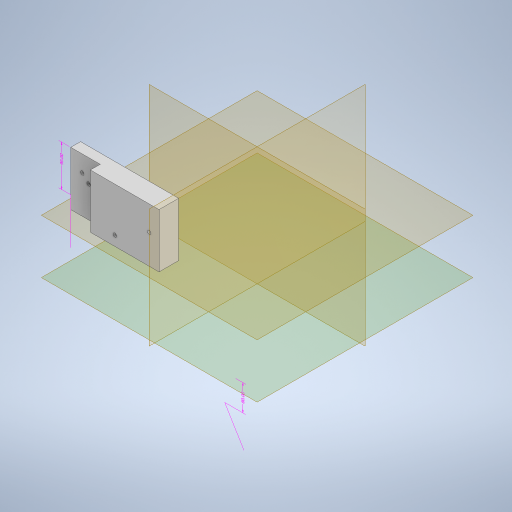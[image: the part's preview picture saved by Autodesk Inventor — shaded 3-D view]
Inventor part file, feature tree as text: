
AUTODESK INVENTOR PART (.ipt)
format: ipt  version: 2023 (Build 270158000, 158)  size: 438,272 bytes
history: native  units: mm
features: sketch x9, other x5, extrude x5, split x5, hole x4, plane x4
ambient origin geometry x8: Origin, YZ Plane, XZ Plane, XY Plane, X Axis, Y Axis, Z Axis, Center Point
bodies: Body1 (feature_tree)
feature tree (32):
  other  "Sólido1"
  other  "Anotaciones"
  extrude  "Extrusión1"  Depth=200.0mm
  hole  "Agujero1"  [1 undecoded]
  extrude  "Extrusión2"  Depth=15.0mm
  extrude  "Extrusión3"  Depth=20.0mm TaperAngle=0.0deg
  extrude  "Extrusión4"  Depth=200.0mm
  extrude  "Extrusión5"  Depth=20.0mm
  hole  "Agujero2"  [1 undecoded]
  plane  "Plano de trabajo1"
  split  "Dividir1"
  plane  "Plano de trabajo2"
  plane  "Plano de trabajo3"
  sketch  "Boceto9"  dims[d37=20.0mm d38=20.0mm]
  plane  "Plano de trabajo4"
  hole  "Agujero3"  [1 undecoded]
  hole  "Agujero4"  [1 undecoded]
  split  "Dividir2"
  split  "Dividir3"
  split  "Dividir4"
  split  "Dividir5"
  other  "Suprimir cara6"
  sketch  "Boceto2"  dims[d7=15.0mm d8=200.0mm]
  sketch  "Boceto3"  dims[d9=10.0mm d10=0.0mm]
  sketch  "Boceto4"  dims[d12=1.75mm d13=1.75mm d14=1.75mm d15=1.75mm d16=10.0mm d17=10.0mm d19=30.0mm]
  sketch  "Boceto5"  dims[d20=3.5mm d21=6.0mm d22=4.0mm d23=2.0mm d24=90.0deg d25=8.0mm d26=20.594885mm d27=15.0mm]
  sketch  "Boceto6"  dims[d28=20.0mm d29=80.0mm d30=0.0mm]
  sketch  "Boceto7"  dims[d31=48.0mm d32=200.0mm]
  sketch  "Boceto8"  dims[d33=110.0mm d34=0.0mm d36=20.0mm]
  sketch  "Boceto10"  dims[d39=90.0mm d40=0.0mm d42=10.0mm d43=30.0mm d44=0.0mm d46=1.75mm d47=1.75mm d48=1.75mm d49=1.75mm d50=10.0mm d51=10.0mm d52=15.0mm d56=3.5mm d57=6.0mm d58=4.0mm d59=2.0mm d60=90.0deg d61=8.0mm d62=20.594885mm d63=10.0mm d65=10.0mm d66=10.0mm d67=31.75mm d70=15.0mm d74=200.0mm d78=20.0mm d82=90.0deg d83=10.0mm d84=30.0mm d85=5.0mm d86=5.0mm d87=5.0mm d88=5.0mm d89=20.0mm d91=30.0mm d92=5.0mm d93=5.0mm d94=3.5mm d95=5.0mm d96=5.0mm d97=5.0mm d98=5.0mm d99=5.0mm d100=20.0mm d101=3.5mm d102=6.0mm d103=4.0mm d104=2.0mm d105=90.0deg d106=8.0mm d107=20.594885mm d108=10.0mm d109=30.0mm d110=5.0mm d111=5.0mm d112=5.0mm d113=5.0mm d114=5.0mm d115=5.0mm d116=3.5mm d117=5.0mm d118=5.0mm d119=5.0mm d120=5.0mm d121=5.0mm d122=30.0mm d123=30.0mm d124=3.5mm d125=6.0mm d126=4.0mm d127=2.0mm d128=90.0deg d129=8.0mm d130=20.594885mm d75=1.454734mm d76=6.982969mm d77=80.0mm d79=4.097996mm d80=1.406125mm d81=90.0mm]
  other  "Cota lineal 2"
  other  "Cota lineal 3"
note: 4 required parameter values undecoded (feature->parameter linkage not recoverable at this tier; creation-order binding heuristic only, values carry confidence <= 0.55)
